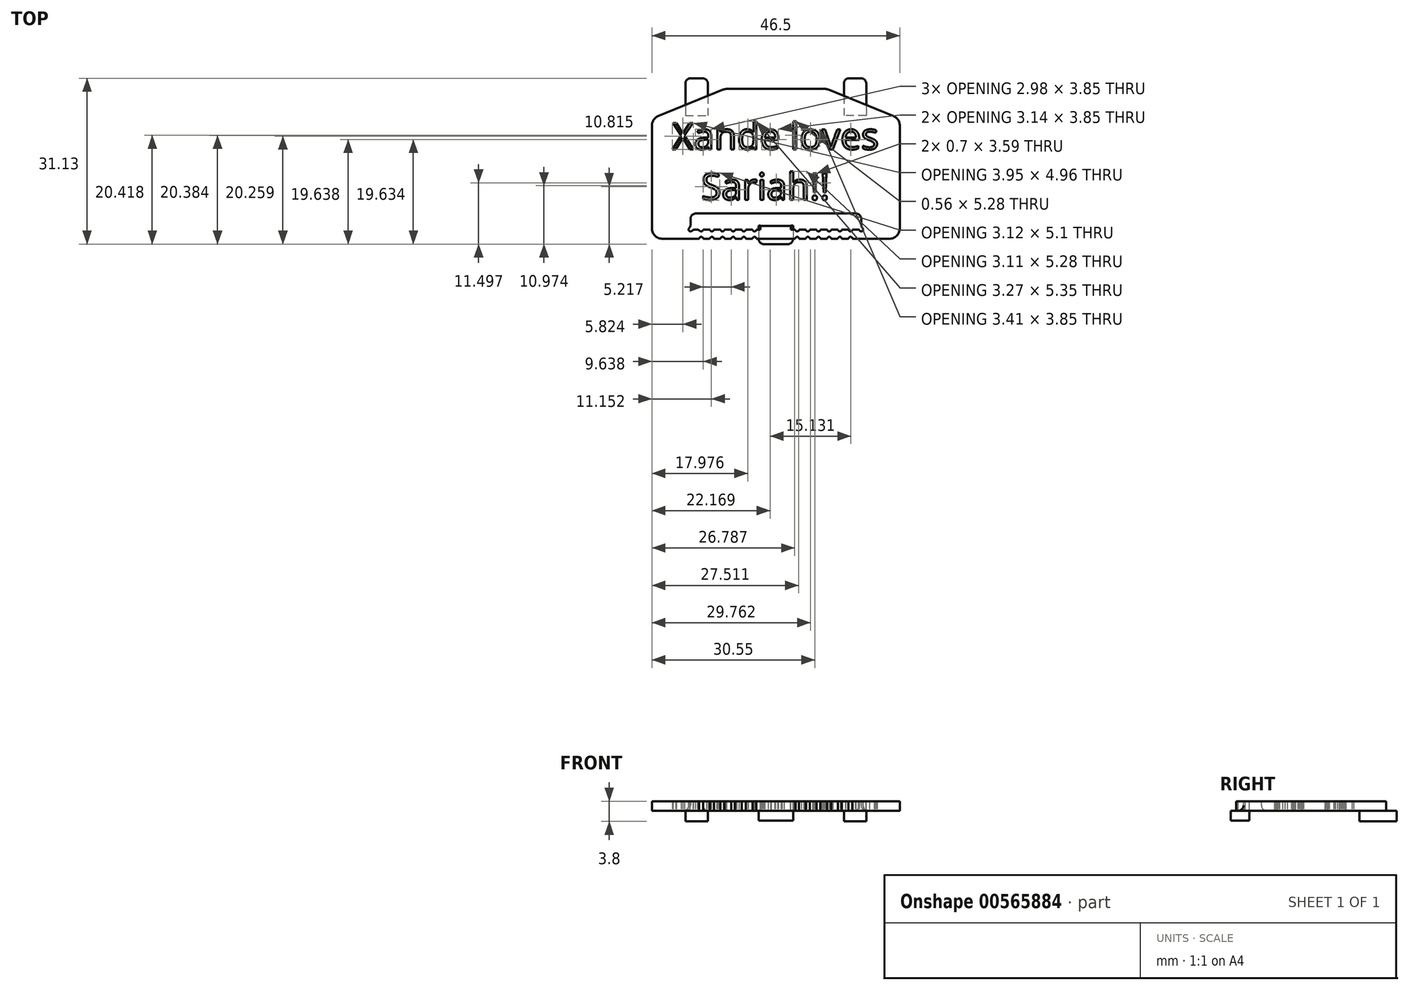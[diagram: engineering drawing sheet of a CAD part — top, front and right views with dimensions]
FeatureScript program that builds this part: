
annotation { "Feature Type Name" : "Feature", "Feature Type Description" : "" }
export const myFeature = defineFeature(function(context is Context, id is Id, definition is map)
    precondition{}
    {
        {
            var Q0;
            Q0=qCreatedBy(makeId("Top.planeOp"),FACE);
            var sketch = newSketch(context, id + "F0", { "sketchPlane" : qUnion([Q0])});
            skLineSegment(sketch, "E0.bottom", {"start": v(0, -22.56) * mm, "end": v(46.5, -22.56) * mm});
            skLineSegment(sketch, "E0.top", {"start": v(13.75, 5.57) * mm, "end": v(32.75, 5.57) * mm});
            skLineSegment(sketch, "E0.left", {"start": v(0, -22.56) * mm, "end": v(0, 0) * mm});
            skLineSegment(sketch, "E0.right", {"start": v(46.5, -22.56) * mm, "end": v(46.5, 0) * mm});
            skLineSegment(sketch, "E1", {"start": v(0, 0) * mm, "end": v(13.75, 5.57) * mm});
            skLineSegment(sketch, "E2", {"start": v(46.5, 0) * mm, "end": v(32.75, 5.57) * mm});
            skSolve(sketch);
        }
        {
            var Q0;
            Q0=makeQuery(id+"F0.imprint","IMPRINT",FACE,{"disambiguationData":[TD([[makeQuery(id+"F0.imprint","IMPRINT",EDGE,{"derivedFrom":sQuery(id+"F0.wireOp",EDGE,"E0.bottom")}),1.0]])]});
            extrude(context, id + "F1", {"entities" : qUnion([Q0]), "depth" : 1.8 * mm, "offsetDistance" : 25.4 * mm});
        }
        {
            var Q0;
            Q0=makeQuery(id+"F1.opExtrude","CAP_FACE",FACE,{"disambiguationData":[OSD([sQuery(id+"F0.wireOp",EDGE,"E0.bottom"),sQuery(id+"F0.wireOp",EDGE,"E0.top"),sQuery(id+"F0.wireOp",EDGE,"E0.left"),sQuery(id+"F0.wireOp",EDGE,"E0.right"),sQuery(id+"F0.wireOp",EDGE,"E1"),sQuery(id+"F0.wireOp",EDGE,"E2")])],"isStart":false});
            var sketch = newSketch(context, id + "F2", { "sketchPlane" : qUnion([Q0])});
            skLineSegment(sketch, "E3.bottom", {"start": v(7.62, -20.8) * mm, "end": v(8.88, -20.8) * mm});
            skLineSegment(sketch, "E3.top", {"start": v(7.25, -17.8) * mm, "end": v(39.25, -17.8) * mm});
            skLineSegment(sketch, "E3.left", {"start": v(7.25, -20.44) * mm, "end": v(7.25, -17.8) * mm});
            skLineSegment(sketch, "E3.right", {"start": v(39.25, -20.44) * mm, "end": v(39.25, -17.8) * mm});
            skLineSegment(sketch, "E4", {"start": v(7.25, -19.3) * mm, "end": v(0, -19.3) * mm, "construction": true});
            skLineSegment(sketch, "E5", {"start": v(39.25, -19.3) * mm, "end": v(46.5, -19.3) * mm, "construction": true});
            skLineSegment(sketch, "E6", {"start": v(23.25, 5.57) * mm, "end": v(23.25, -22.56) * mm, "construction": true});
            skLineSegment(sketch, "E7", {"start": v(20.36, -20.11) * mm, "end": v(26.03, -20.11) * mm});
            skLineSegment(sketch, "E8", {"start": v(26.03, -20.8) * mm, "end": v(26.88, -20.8) * mm});
            skLineSegment(sketch, "E9", {"start": v(20.36, -20.8) * mm, "end": v(20.36, -20.11) * mm});
            skLineSegment(sketch, "E10", {"start": v(26.03, -20.8) * mm, "end": v(26.03, -20.11) * mm});
            skArc(sketch, "E11", {"start": v(7.25, -20.44) * mm, "mid": v(7, -21.07) * mm, "end": v(7.62, -20.8) * mm});
            skArc(sketch, "E12", {"start": v(8.88, -20.8) * mm, "mid": v(9.25, -21.18) * mm, "end": v(9.62, -20.8) * mm});
            skArc(sketch, "E13", {"start": v(10.88, -20.8) * mm, "mid": v(11.25, -21.18) * mm, "end": v(11.62, -20.8) * mm});
            skArc(sketch, "E14", {"start": v(12.88, -20.8) * mm, "mid": v(13.25, -21.18) * mm, "end": v(13.62, -20.8) * mm});
            skArc(sketch, "E15", {"start": v(14.88, -20.8) * mm, "mid": v(15.25, -21.18) * mm, "end": v(15.62, -20.8) * mm});
            skArc(sketch, "E16", {"start": v(16.88, -20.8) * mm, "mid": v(17.25, -21.18) * mm, "end": v(17.62, -20.8) * mm});
            skArc(sketch, "E17", {"start": v(18.88, -20.8) * mm, "mid": v(19.25, -21.18) * mm, "end": v(19.62, -20.8) * mm});
            skLineSegment(sketch, "E18.trimOffspring", {"start": v(9.62, -20.8) * mm, "end": v(10.88, -20.8) * mm});
            skLineSegment(sketch, "E19.trimOffspring", {"start": v(11.62, -20.8) * mm, "end": v(12.88, -20.8) * mm});
            skLineSegment(sketch, "E20.trimOffspring", {"start": v(13.62, -20.8) * mm, "end": v(14.88, -20.8) * mm});
            skLineSegment(sketch, "E21.trimOffspring", {"start": v(15.62, -20.8) * mm, "end": v(16.88, -20.8) * mm});
            skLineSegment(sketch, "E22.trimOffspring", {"start": v(17.62, -20.8) * mm, "end": v(18.88, -20.8) * mm});
            skLineSegment(sketch, "E23.trimOffspring", {"start": v(19.62, -20.8) * mm, "end": v(20.36, -20.8) * mm});
            skArc(sketch, "E24.MirrorCS", {"start": v(39.25, -20.44) * mm, "mid": v(39.5, -21.07) * mm, "end": v(38.88, -20.81) * mm});
            skArc(sketch, "E25.MirrorCS", {"start": v(37.62, -20.81) * mm, "mid": v(37.25, -21.18) * mm, "end": v(36.88, -20.81) * mm});
            skArc(sketch, "E26.MirrorCS", {"start": v(35.62, -20.8) * mm, "mid": v(35.25, -21.18) * mm, "end": v(34.88, -20.8) * mm});
            skArc(sketch, "E27.MirrorCS", {"start": v(33.62, -20.8) * mm, "mid": v(33.25, -21.18) * mm, "end": v(32.88, -20.8) * mm});
            skArc(sketch, "E28.MirrorCS", {"start": v(31.62, -20.8) * mm, "mid": v(31.25, -21.18) * mm, "end": v(30.88, -20.8) * mm});
            skArc(sketch, "E29.MirrorCS", {"start": v(29.62, -20.8) * mm, "mid": v(29.25, -21.18) * mm, "end": v(28.88, -20.8) * mm});
            skArc(sketch, "E30.MirrorCS", {"start": v(27.62, -20.8) * mm, "mid": v(27.25, -21.18) * mm, "end": v(26.88, -20.8) * mm});
            skLineSegment(sketch, "E31.trimOffspring", {"start": v(27.62, -20.8) * mm, "end": v(28.88, -20.8) * mm});
            skLineSegment(sketch, "E32.trimOffspring", {"start": v(29.62, -20.8) * mm, "end": v(30.88, -20.8) * mm});
            skLineSegment(sketch, "E33.trimOffspring", {"start": v(33.62, -20.8) * mm, "end": v(34.88, -20.8) * mm});
            skLineSegment(sketch, "E34.trimOffspring", {"start": v(35.62, -20.8) * mm, "end": v(36.88, -20.8) * mm});
            skLineSegment(sketch, "E35.trimOffspring", {"start": v(37.62, -20.8) * mm, "end": v(38.88, -20.8) * mm});
            skPoint(sketch, "E36.orphan", {"position": v(39.25, -20.8) * mm});
            skLineSegment(sketch, "E37", {"start": v(32.88, -20.8) * mm, "end": v(31.62, -20.8) * mm});
            skLineSegment(sketch, "E38", {"start": v(39.5, -21.68) * mm, "end": v(7.3, -21.68) * mm, "construction": true});
            skPoint(sketch, "E38.startSnap0", {"position": v(39.5, -21.07) * mm});
            skLineSegment(sketch, "E39", {"start": v(16.18, -21.68) * mm, "end": v(16.18, -20.8) * mm, "construction": true});
            skLineSegment(sketch, "E40", {"start": v(16.18, -21.68) * mm, "end": v(16.18, -22.56) * mm, "construction": true});
            skArc(sketch, "E41.MirrorCS", {"start": v(37.62, -22.56) * mm, "mid": v(37.25, -22.2) * mm, "end": v(36.88, -22.56) * mm});
            skArc(sketch, "E42.MirrorCS", {"start": v(35.62, -22.56) * mm, "mid": v(35.25, -22.2) * mm, "end": v(34.88, -22.56) * mm});
            skArc(sketch, "E43.MirrorCS", {"start": v(33.62, -22.56) * mm, "mid": v(33.25, -22.2) * mm, "end": v(32.88, -22.56) * mm});
            skArc(sketch, "E44.MirrorCS", {"start": v(31.62, -22.56) * mm, "mid": v(31.25, -22.2) * mm, "end": v(30.88, -22.56) * mm});
            skArc(sketch, "E45.MirrorCS", {"start": v(29.62, -22.56) * mm, "mid": v(29.25, -22.2) * mm, "end": v(28.88, -22.56) * mm});
            skArc(sketch, "E46.MirrorCS", {"start": v(27.62, -22.56) * mm, "mid": v(27.25, -22.2) * mm, "end": v(26.88, -22.56) * mm});
            skArc(sketch, "E47.MirrorCS", {"start": v(8.88, -22.56) * mm, "mid": v(9.25, -22.2) * mm, "end": v(9.62, -22.56) * mm});
            skArc(sketch, "E48.MirrorCS", {"start": v(10.88, -22.56) * mm, "mid": v(11.25, -22.2) * mm, "end": v(11.62, -22.56) * mm});
            skArc(sketch, "E49.MirrorCS", {"start": v(12.88, -22.56) * mm, "mid": v(13.25, -22.2) * mm, "end": v(13.62, -22.56) * mm});
            skArc(sketch, "E50.MirrorCS", {"start": v(14.88, -22.56) * mm, "mid": v(15.25, -22.2) * mm, "end": v(15.62, -22.56) * mm});
            skArc(sketch, "E51.MirrorCS", {"start": v(16.88, -22.56) * mm, "mid": v(17.25, -22.2) * mm, "end": v(17.62, -22.56) * mm});
            skArc(sketch, "E52.MirrorCS", {"start": v(18.88, -22.56) * mm, "mid": v(19.25, -22.2) * mm, "end": v(19.62, -22.56) * mm});
            skLineSegment(sketch, "E53", {"start": v(8.88, -22.56) * mm, "end": v(37.62, -22.56) * mm});
            skSolve(sketch);
        }
        {
            var Q0;
            Q0 = qSketchRegion(id + "F2", true);
            extrude(context, id + "F3", {"entities" : qUnion([Q0]), "operationType" : NewBodyOperationType.REMOVE, "oppositeDirection" : true, "depth" : 25.4 * mm, "offsetDistance" : 25.4 * mm});
        }
        {
            var Q0;
            Q0=makeQuery(id+"F0.imprint","IMPRINT",FACE,{"disambiguationData":[TD([[makeQuery(id+"F0.imprint","IMPRINT",EDGE,{"derivedFrom":sQuery(id+"F0.wireOp",EDGE,"E0.bottom")}),1.0]])]});
            var sketch = newSketch(context, id + "F4", { "sketchPlane" : qUnion([Q0])});
            skLineSegment(sketch, "E54.bottom", {"start": v(20.02, -20.1) * mm, "end": v(26.49, -20.1) * mm});
            skLineSegment(sketch, "E54.top", {"start": v(20.02, -23.56) * mm, "end": v(26.49, -23.56) * mm});
            skLineSegment(sketch, "E54.left", {"start": v(20.02, -20.1) * mm, "end": v(20.02, -23.56) * mm});
            skLineSegment(sketch, "E54.right", {"start": v(26.49, -20.1) * mm, "end": v(26.49, -23.56) * mm});
            skLineSegment(sketch, "E55", {"start": v(20.02, -16.96) * mm, "end": v(0, -16.96) * mm, "construction": true});
            skLineSegment(sketch, "E56", {"start": v(26.49, -16.96) * mm, "end": v(46.5, -16.96) * mm, "construction": true});
            skSolve(sketch);
        }
        {
            var Q0;
            Q0 = qSketchRegion(id + "F4", true);
            extrude(context, id + "F5", {"entities" : qUnion([Q0]), "operationType" : NewBodyOperationType.ADD, "oppositeDirection" : true, "depth" : 1.84 * mm, "offsetDistance" : 25.4 * mm});
        }
        {
            var Q0;
            Q0=makeQuery(id+"F0.imprint","IMPRINT",FACE,{"disambiguationData":[TD([[makeQuery(id+"F0.imprint","IMPRINT",EDGE,{"derivedFrom":sQuery(id+"F0.wireOp",EDGE,"E0.bottom")}),1.0]])]});
            var sketch = newSketch(context, id + "F6", { "sketchPlane" : qUnion([Q0])});
            skLineSegment(sketch, "E57.bottom", {"start": v(6.3, 7.57) * mm, "end": v(10.5, 7.57) * mm});
            skLineSegment(sketch, "E57.top", {"start": v(6.3, 0.57) * mm, "end": v(10.5, 0.57) * mm});
            skLineSegment(sketch, "E57.left", {"start": v(6.3, 7.57) * mm, "end": v(6.3, 0.57) * mm});
            skLineSegment(sketch, "E57.right", {"start": v(10.5, 7.57) * mm, "end": v(10.5, 0.57) * mm});
            skLineSegment(sketch, "E58", {"start": v(23.25, 5.57) * mm, "end": v(23.25, -20.77) * mm, "construction": true});
            skLineSegment(sketch, "E59.MirrorCS", {"start": v(40.2, 7.57) * mm, "end": v(36, 7.57) * mm});
            skLineSegment(sketch, "E60.MirrorCS", {"start": v(36, 7.57) * mm, "end": v(36, 0.57) * mm});
            skLineSegment(sketch, "E61.MirrorCS", {"start": v(40.2, 7.57) * mm, "end": v(40.2, 0.57) * mm});
            skLineSegment(sketch, "E62.MirrorCS", {"start": v(40.2, 0.57) * mm, "end": v(36, 0.57) * mm});
            skSolve(sketch);
        }
        {
            var Q0;
            Q0 = qSketchRegion(id + "F6", true);
            extrude(context, id + "F7", {"entities" : qUnion([Q0]), "oppositeDirection" : true, "depth" : 2 * mm, "offsetDistance" : 25.4 * mm});
        }
        {
            var Q0;
            Q0=makeQuery(id+"F1.opExtrude","SWEPT_EDGE",EDGE,{"disambiguationData":[OSD([sQuery(id+"F0.wireOp",EDGE,"E0.right"),sQuery(id+"F0.wireOp",EDGE,"E2")])]});
            var Q1;
            Q1=makeQuery(id+"F1.opExtrude","SWEPT_EDGE",EDGE,{"disambiguationData":[OSD([sQuery(id+"F0.wireOp",EDGE,"E0.top"),sQuery(id+"F0.wireOp",EDGE,"E2")])]});
            var Q2;
            Q2=makeQuery(id+"F1.opExtrude","SWEPT_EDGE",EDGE,{"disambiguationData":[OSD([sQuery(id+"F0.wireOp",EDGE,"E0.top"),sQuery(id+"F0.wireOp",EDGE,"E1")])]});
            var Q3;
            Q3=makeQuery(id+"F1.opExtrude","SWEPT_EDGE",EDGE,{"disambiguationData":[OSD([sQuery(id+"F0.wireOp",EDGE,"E0.left"),sQuery(id+"F0.wireOp",EDGE,"E1")])]});
            var Q4;
            Q4=makeQuery(id+"F1.opExtrude","SWEPT_EDGE",EDGE,{"disambiguationData":[OSD([sQuery(id+"F0.wireOp",EDGE,"E0.bottom"),sQuery(id+"F0.wireOp",EDGE,"E0.right")])]});
            var Q5;
            Q5=makeQuery(id+"F1.opExtrude","SWEPT_EDGE",EDGE,{"disambiguationData":[OSD([sQuery(id+"F0.wireOp",EDGE,"E0.bottom"),sQuery(id+"F0.wireOp",EDGE,"E0.left")])]});
            fillet(context, id + "F8", {"entities" : qUnion([Q0, Q1, Q2, Q3, Q4, Q5]), "radius" : 2 * mm, "tangentPropagation" : true, "allowEdgeOverflow" : false});
        }
        {
            var Q0;
            Q0=makeQuery(id+"F0.imprint","IMPRINT",FACE,{"disambiguationData":[TD([[makeQuery(id+"F0.imprint","IMPRINT",EDGE,{"derivedFrom":sQuery(id+"F0.wireOp",EDGE,"E0.bottom")}),1.0]])]});
            var sketch = newSketch(context, id + "F9", { "sketchPlane" : qUnion([Q0])});
            skText(sketch, "E63", { "text": "Xande loves\n   Sariah!!", "fontName": "OpenSans-Regular.ttf"});
            skLineSegment(sketch, "E64", {"start": v(0, -3.02) * mm, "end": v(3.82, -3.02) * mm, "construction": true});
            skLineSegment(sketch, "E65", {"start": v(42.68, -3.28) * mm, "end": v(46.5, -3.28) * mm, "construction": true});
            const initialGuessF9  = {"E63": [0.00382, -0.00578, 1, 0, 0.005]};
            skSetInitialGuess(sketch, initialGuessF9);
            skSolve(sketch);
        }
        {
            var Q0;
            Q0 = qSketchRegion(id + "F9", true);
            extrude(context, id + "F10", {"entities" : qUnion([Q0]), "operationType" : NewBodyOperationType.REMOVE, "depth" : 25.4 * mm, "offsetDistance" : 25.4 * mm});
        }
        {
            var Q0;
            Q0=makeQuery(id+"F3.boolean.opBoolean","COPY",EDGE,{"derivedFrom":makeQuery(id+"F3.opExtrude","SWEPT_EDGE",EDGE,{"disambiguationData":[OSD([sQuery(id+"F2.wireOp",EDGE,"E3.top"),sQuery(id+"F2.wireOp",EDGE,"E3.left")])]})});
            var Q1;
            Q1=makeQuery(id+"F3.boolean.opBoolean","COPY",EDGE,{"derivedFrom":makeQuery(id+"F3.opExtrude","SWEPT_EDGE",EDGE,{"disambiguationData":[OSD([sQuery(id+"F2.wireOp",EDGE,"E3.top"),sQuery(id+"F2.wireOp",EDGE,"E3.right")])]})});
            var Q2;
            Q2=makeQuery(id+"F3.boolean.opBoolean","COPY",EDGE,{"derivedFrom":makeQuery(id+"F3.opExtrude","SWEPT_EDGE",EDGE,{"disambiguationData":[OSD([sQuery(id+"F2.wireOp",EDGE,"E3.bottom"),sQuery(id+"F2.wireOp",EDGE,"E3.left")])]})});
            var Q3;
            Q3=makeQuery(id+"F3.boolean.opBoolean","COPY",EDGE,{"derivedFrom":makeQuery(id+"F3.opExtrude","SWEPT_EDGE",EDGE,{"disambiguationData":[OSD([sQuery(id+"F2.wireOp",EDGE,"E3.bottom"),sQuery(id+"F2.wireOp",EDGE,"E3.right")])]})});
            fillet(context, id + "F11", {"entities" : qUnion([Q0, Q1, Q2, Q3]), "radius" : 1 * mm, "tangentPropagation" : true, "allowEdgeOverflow" : false});
        }
        {
            var Q0;
            Q0=makeQuery(id+"F5.opExtrude","SWEPT_EDGE",EDGE,{"disambiguationData":[OSD([sQuery(id+"F4.wireOp",EDGE,"E54.top"),sQuery(id+"F4.wireOp",EDGE,"E54.left")])]});
            var Q1;
            Q1=makeQuery(id+"F5.opExtrude","SWEPT_EDGE",EDGE,{"disambiguationData":[OSD([sQuery(id+"F4.wireOp",EDGE,"E54.top"),sQuery(id+"F4.wireOp",EDGE,"E54.right")])]});
            fillet(context, id + "F12", {"entities" : qUnion([Q0, Q1]), "radius" : 1 * mm, "tangentPropagation" : true, "allowEdgeOverflow" : false});
        }
        {
            var Q0;
            Q0=makeQuery(id+"F7.opExtrude","SWEPT_EDGE",EDGE,{"disambiguationData":[OSD([sQuery(id+"F6.wireOp",EDGE,"E57.bottom"),sQuery(id+"F6.wireOp",EDGE,"E57.left")])]});
            var Q1;
            Q1=makeQuery(id+"F7.opExtrude","SWEPT_EDGE",EDGE,{"disambiguationData":[OSD([sQuery(id+"F6.wireOp",EDGE,"E57.bottom"),sQuery(id+"F6.wireOp",EDGE,"E57.right")])]});
            var Q2;
            Q2=makeQuery(id+"F7.opExtrude","SWEPT_EDGE",EDGE,{"disambiguationData":[OSD([sQuery(id+"F6.wireOp",EDGE,"E59.MirrorCS"),sQuery(id+"F6.wireOp",EDGE,"E60.MirrorCS")])]});
            var Q3;
            Q3=makeQuery(id+"F7.opExtrude","SWEPT_EDGE",EDGE,{"disambiguationData":[OSD([sQuery(id+"F6.wireOp",EDGE,"E59.MirrorCS"),sQuery(id+"F6.wireOp",EDGE,"E61.MirrorCS")])]});
            fillet(context, id + "F13", {"entities" : qUnion([Q0, Q1, Q2, Q3]), "radius" : 1 * mm, "tangentPropagation" : true, "allowEdgeOverflow" : false});
        }
        {
            var Q0;
            {var subQ0=makeQuery(id+"F3.opExtrude","SWEPT_FACE",FACE,{"disambiguationData":[OSD([sQuery(id+"F2.wireOp",EDGE,"E3.bottom")])]});Q0=makeQuery(id+"F5.boolean.opBoolean","SPLIT",EDGE,{"disambiguationData":[topologyDisambiguationEdgeConnected([makeQuery(id+"F3.boolean.opBoolean","COPY",FACE,{"derivedFrom":subQ0}),makeQuery(id+"F5.opExtrude","CAP_FACE",FACE,{"disambiguationData":[OSD([sQuery(id+"F4.wireOp",EDGE,"E54.bottom"),sQuery(id+"F4.wireOp",EDGE,"E54.top"),sQuery(id+"F4.wireOp",EDGE,"E54.left"),sQuery(id+"F4.wireOp",EDGE,"E54.right")])],"isStart":true})])],"derivedFrom":makeQuery(id+"F3.boolean.opBoolean","INTERSECT",EDGE,{"derivedFrom":[makeQuery(id+"F1.opExtrude","CAP_FACE",FACE,{"disambiguationData":[OSD([sQuery(id+"F0.wireOp",EDGE,"E0.bottom"),sQuery(id+"F0.wireOp",EDGE,"E0.top"),sQuery(id+"F0.wireOp",EDGE,"E0.left"),sQuery(id+"F0.wireOp",EDGE,"E0.right"),sQuery(id+"F0.wireOp",EDGE,"E1"),sQuery(id+"F0.wireOp",EDGE,"E2")])],"isStart":true}),subQ0]})});}
            fillet(context, id + "F14", {"entities" : qUnion([Q0]), "radius" : 1 * mm, "tangentPropagation" : true, "allowEdgeOverflow" : false});
        }
    });
